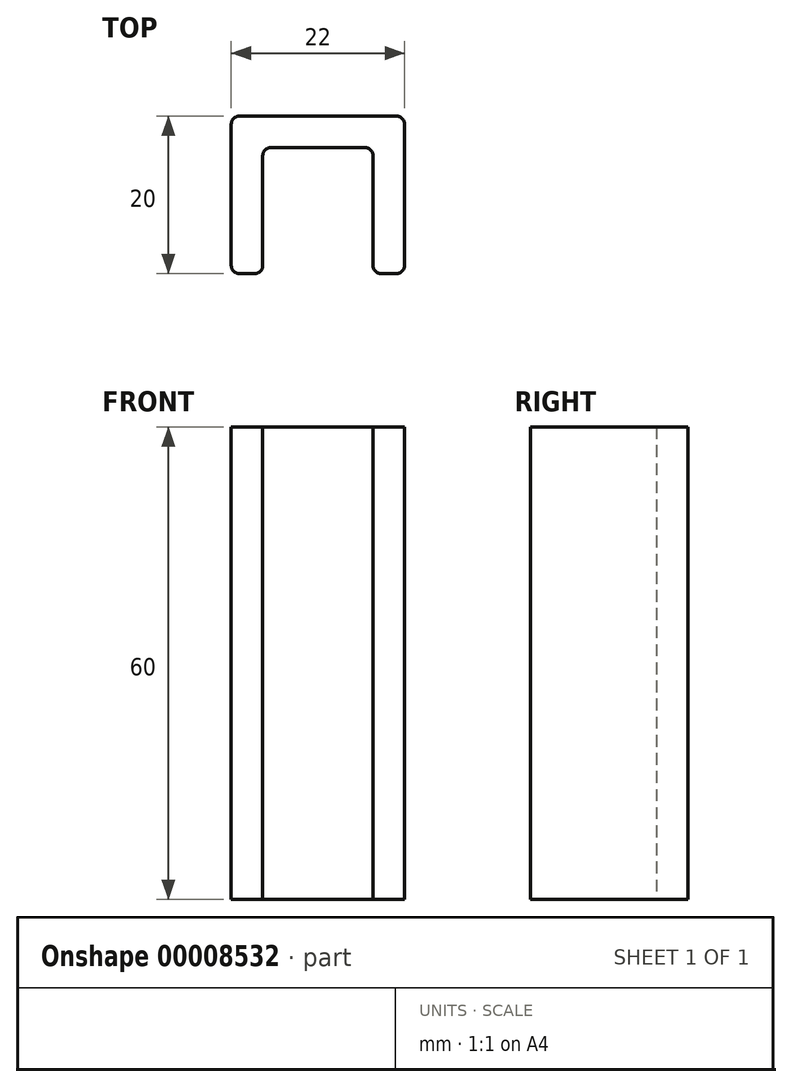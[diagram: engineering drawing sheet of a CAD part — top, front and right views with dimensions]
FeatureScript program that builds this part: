
annotation { "Feature Type Name" : "Feature", "Feature Type Description" : "" }
export const myFeature = defineFeature(function(context is Context, id is Id, definition is map)
    precondition{}
    {
        {
            var Q0;
            Q0=qCreatedBy(makeId("Top.planeOp"),FACE);
            var sketch = newSketch(context, id + "F0", { "sketchPlane" : qUnion([Q0])});
            skLineSegment(sketch, "E0.bottom", {"start": v(7, 8) * mm, "end": v(-7, 8) * mm});
            skLineSegment(sketch, "E0.left", {"start": v(7, 8) * mm, "end": v(7, -8) * mm});
            skLineSegment(sketch, "E0.right", {"start": v(-7, 8) * mm, "end": v(-7, -8) * mm});
            skPoint(sketch, "E0.middle", {"position": v(0, 0) * mm});
            skLineSegment(sketch, "E1.0", {"start": v(11, 12) * mm, "end": v(-11, 12) * mm});
            skLineSegment(sketch, "E1.1", {"start": v(11, 12) * mm, "end": v(11, -8) * mm});
            skLineSegment(sketch, "E1.3", {"start": v(-11, 12) * mm, "end": v(-11, -8) * mm});
            skLineSegment(sketch, "E2", {"start": v(-7, -8) * mm, "end": v(-11, -8) * mm});
            skLineSegment(sketch, "E3", {"start": v(7, -8) * mm, "end": v(11, -8) * mm});
            skSolve(sketch);
        }
        {
            var Q0;
            Q0 = qSketchRegion(id + "F0", true);
            extrude(context, id + "F1", {"entities" : qUnion([Q0]), "depth" : 60 * mm, "offsetDistance" : 25 * mm});
        }
        {
            var Q0;
            Q0=makeQuery(id+"F1.opExtrude","SWEPT_EDGE",EDGE,{"disambiguationData":[OSD([sQuery(id+"F0.wireOp",EDGE,"E1.0"),sQuery(id+"F0.wireOp",EDGE,"E1.3")])]});
            var Q1;
            Q1=makeQuery(id+"F1.opExtrude","SWEPT_EDGE",EDGE,{"disambiguationData":[OSD([sQuery(id+"F0.wireOp",EDGE,"E1.0"),sQuery(id+"F0.wireOp",EDGE,"E1.1")])]});
            var Q2;
            Q2=makeQuery(id+"F1.opExtrude","SWEPT_EDGE",EDGE,{"disambiguationData":[OSD([sQuery(id+"F0.wireOp",EDGE,"E1.1"),sQuery(id+"F0.wireOp",EDGE,"E3")])]});
            var Q3;
            Q3=makeQuery(id+"F1.opExtrude","SWEPT_EDGE",EDGE,{"disambiguationData":[OSD([sQuery(id+"F0.wireOp",EDGE,"E0.left"),sQuery(id+"F0.wireOp",EDGE,"E3")])]});
            var Q4;
            Q4=makeQuery(id+"F1.opExtrude","SWEPT_EDGE",EDGE,{"disambiguationData":[OSD([sQuery(id+"F0.wireOp",EDGE,"E0.right"),sQuery(id+"F0.wireOp",EDGE,"E2")])]});
            var Q5;
            Q5=makeQuery(id+"F1.opExtrude","SWEPT_EDGE",EDGE,{"disambiguationData":[OSD([sQuery(id+"F0.wireOp",EDGE,"E1.3"),sQuery(id+"F0.wireOp",EDGE,"E2")])]});
            var Q6;
            Q6=makeQuery(id+"F1.opExtrude","SWEPT_EDGE",EDGE,{"disambiguationData":[OSD([sQuery(id+"F0.wireOp",EDGE,"E0.bottom"),sQuery(id+"F0.wireOp",EDGE,"E0.right")])]});
            var Q7;
            Q7=makeQuery(id+"F1.opExtrude","SWEPT_EDGE",EDGE,{"disambiguationData":[OSD([sQuery(id+"F0.wireOp",EDGE,"E0.bottom"),sQuery(id+"F0.wireOp",EDGE,"E0.left")])]});
            fillet(context, id + "F2", {"entities" : qUnion([Q0, Q1, Q2, Q3, Q4, Q5, Q6, Q7]), "radius" : 1 * mm, "tangentPropagation" : true, "allowEdgeOverflow" : false});
        }
    });
